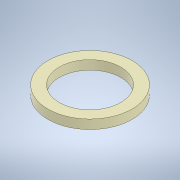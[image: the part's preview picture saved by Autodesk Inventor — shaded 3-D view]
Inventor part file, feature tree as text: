
AUTODESK INVENTOR PART (.ipt)
format: ipt  version: 2022 (Build 260153000, 153)  size: 105,472 bytes
history: native  units: mm
features: extrude x1, sketch x1
ambient origin geometry x8: Origin, YZ Plane, XZ Plane, XY Plane, X Axis, Y Axis, Z Axis, Center Point
bodies: Solid1 (feature_tree)
feature tree (2):
  extrude  "Extrusion1"  Depth=2.7mm
  sketch  "Sketch1"  dims[d0=18.3mm d1=25.0mm d2=2.7mm d3=0.0mm]
